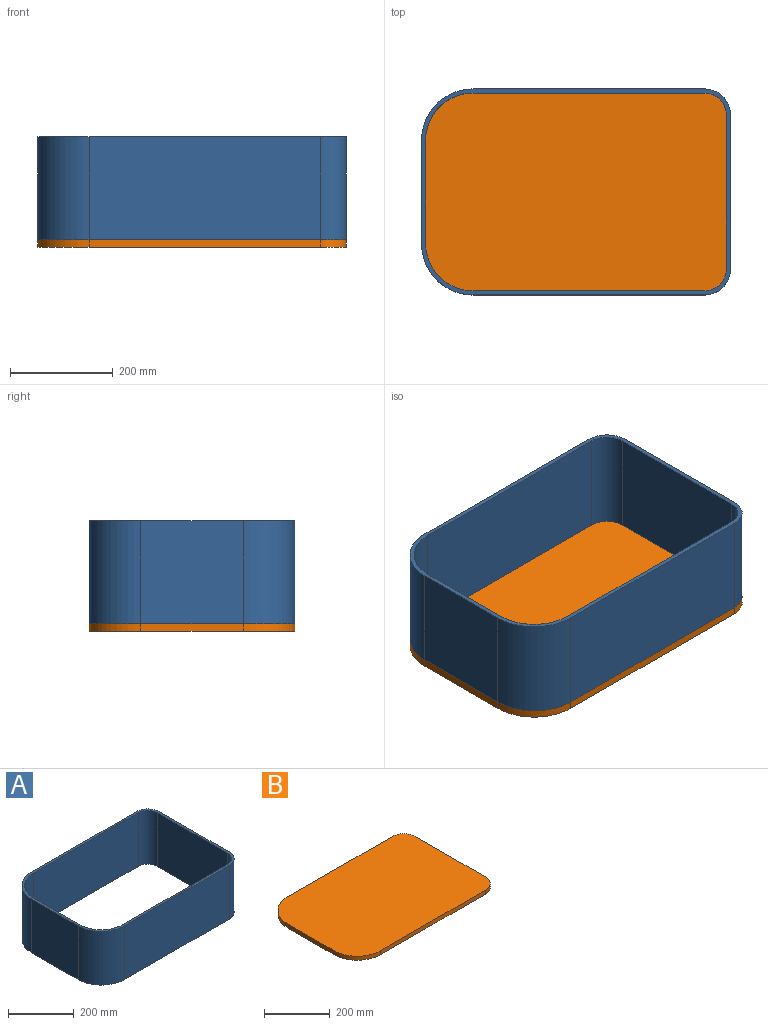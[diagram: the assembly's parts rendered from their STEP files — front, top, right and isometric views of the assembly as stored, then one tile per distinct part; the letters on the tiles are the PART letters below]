
ASSEMBLY  parts=2 mates=1
PART A: 18 faces, bbox 600x400x200 mm
  f0: plane 200x200mm, normal (-1,0,0), area 40000mm2, adj f1,f15,f16,f17
  f1: cylinder r=100mm len=200mm, axis (0,0,-1), area 31415.9mm2, adj f0,f2,f16,f17
  f2: plane 450x200mm, normal (0,-1,0), area 90000mm2, adj f1,f3,f16,f17
  f3: cylinder r=50mm len=200mm, axis (0,0,-1), area 15708mm2, adj f2,f4,f16,f17
  f4: plane 300x200mm, normal (1,0,0), area 60000mm2, adj f3,f5,f16,f17
  f5: cylinder r=50mm len=200mm, axis (0,0,-1), area 15708mm2, adj f4,f6,f16,f17
  f6: plane 450x200mm, normal (0,1,0), area 90000mm2, adj f5,f15,f16,f17
  f7: cylinder r=42mm len=200mm, axis (0,0,-1), area 13194.7mm2, adj f8,f14,f16,f17
  f8: plane 300x200mm, normal (-1,0,0), area 60000mm2, adj f7,f9,f16,f17
  f9: cylinder r=42mm len=200mm, axis (0,0,-1), area 13194.7mm2, adj f8,f10,f16,f17
  f10: plane 450x200mm, normal (0,1,0), area 90000mm2, adj f9,f11,f16,f17
  f11: cylinder r=92mm len=200mm, axis (0,0,-1), area 28902.7mm2, adj f10,f12,f16,f17
  f12: plane 200x200mm, normal (1,0,0), area 40000mm2, adj f11,f13,f16,f17
  f13: cylinder r=92mm len=200mm, axis (0,0,-1), area 28902.7mm2, adj f12,f14,f16,f17
  f14: plane 450x200mm, normal (0,-1,0), area 90000mm2, adj f7,f13,f16,f17
  f15: cylinder r=100mm len=200mm, axis (0,0,-1), area 31415.9mm2, adj f0,f6,f16,f17
  f16: plane 600x400mm, normal (0,0,1), area 14768.8mm2, adj f0,f1,f2,f3,f4,f5,f6,f7
  f17: plane 600x400mm, normal (0,0,-1), area 14768.8mm2, adj f0,f1,f2,f3,f4,f5,f6,f7
PART B: 10 faces, bbox 600x400x15 mm
  f0: plane 200x15mm, normal (-1,0,0), area 3000mm2, adj f1,f7,f8,f9
  f1: cylinder r=100mm len=100mm, axis (0,0,-1), area 2356.2mm2, adj f0,f2,f8,f9
  f2: plane 450x15mm, normal (0,-1,0), area 6750mm2, adj f1,f3,f8,f9
  f3: cylinder r=50mm len=50mm, axis (0,0,-1), area 1178.1mm2, adj f2,f4,f8,f9
  f4: plane 300x15mm, normal (1,0,0), area 4500mm2, adj f3,f5,f8,f9
  f5: cylinder r=50mm len=50mm, axis (0,0,-1), area 1178.1mm2, adj f4,f6,f8,f9
  f6: plane 450x15mm, normal (0,1,0), area 6750mm2, adj f5,f7,f8,f9
  f7: cylinder r=100mm len=100mm, axis (0,0,-1), area 2356.2mm2, adj f0,f6,f8,f9
  f8: plane 600x400mm, normal (0,0,1), area 234635mm2, adj f0,f1,f2,f3,f4,f5,f6,f7
  f9: plane 600x400mm, normal (0,0,-1), area 234635mm2, adj f0,f1,f2,f3,f4,f5,f6,f7
PLACE A t=(0,0,15)mm
PLACE B at identity
MATE fastened A.f17 <-> B.f8  axis (0,0,-1) through (300,0,15)mm
